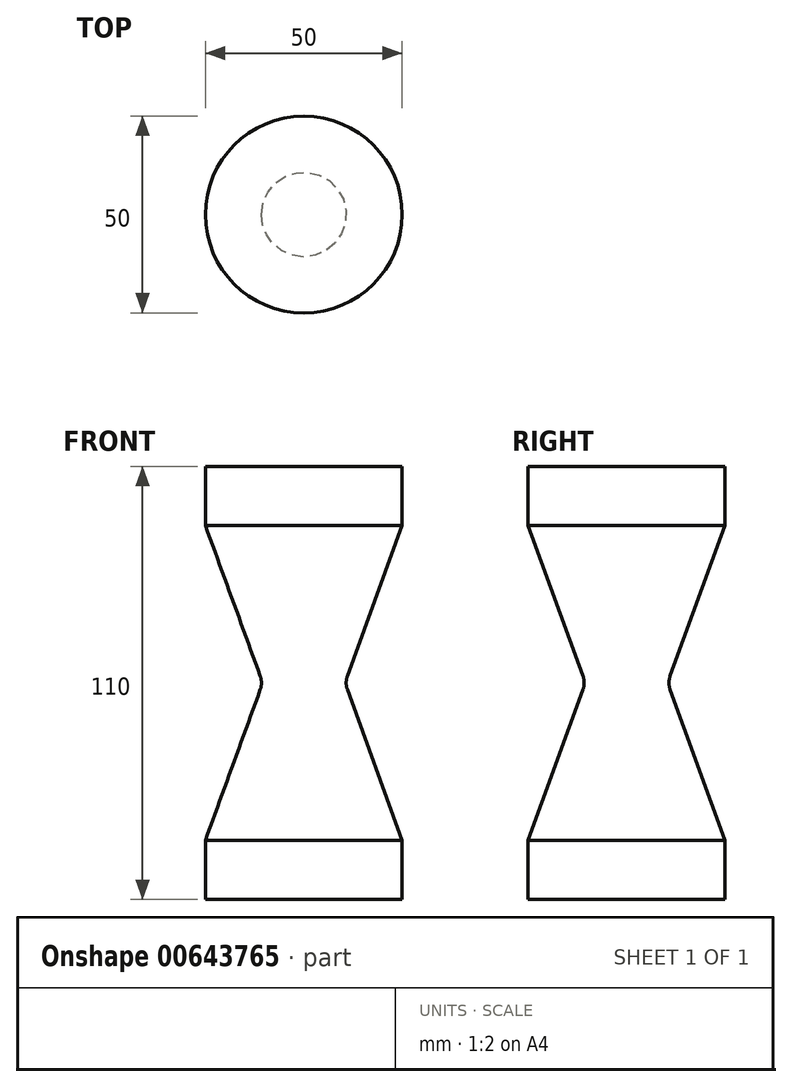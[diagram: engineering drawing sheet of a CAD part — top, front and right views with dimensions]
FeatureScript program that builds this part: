
annotation { "Feature Type Name" : "Feature", "Feature Type Description" : "" }
export const myFeature = defineFeature(function(context is Context, id is Id, definition is map)
    precondition{}
    {
        {
            var Q0;
            Q0=qCreatedBy(makeId("Front.planeOp"),FACE);
            var sketch = newSketch(context, id + "F0", { "sketchPlane" : qUnion([Q0])});
            skLineSegment(sketch, "E0", {"start": v(0, 0) * mm, "end": v(0, 110) * mm});
            skLineSegment(sketch, "E1", {"start": v(0, 0) * mm, "end": v(25, 0) * mm});
            skLineSegment(sketch, "E2", {"start": v(25, 0) * mm, "end": v(25, 15) * mm});
            skLineSegment(sketch, "E3", {"start": v(25, 15) * mm, "end": v(10.44, 55) * mm});
            skPoint(sketch, "E3.endSnap0", {"position": v(0, 55) * mm});
            skLineSegment(sketch, "E4", {"start": v(0, 55) * mm, "end": v(6.55, 55) * mm, "construction": true});
            skLineSegment(sketch, "E5.MirrorCS", {"start": v(25, 95) * mm, "end": v(10.44, 55) * mm});
            skLineSegment(sketch, "E6.MirrorCS", {"start": v(25, 110) * mm, "end": v(25, 95) * mm});
            skLineSegment(sketch, "E7.MirrorCS", {"start": v(0, 110) * mm, "end": v(25, 110) * mm});
            skSolve(sketch);
        }
        {
            var Q0;
            Q0 = qSketchRegion(id + "F0", true);
            var Q1;
            Q1=sQuery(id+"F0.wireOp",EDGE,"E0");
            revolve(context, id + "F1", {"entities" : qUnion([Q0]), "axis" : qUnion([Q1]), "revolveType" : RevolveType.FULL});
        }
        {
            var Q0;
            Q0=makeQuery(id+"F1.opRevolve","SWEPT_EDGE",EDGE,{"disambiguationData":[OSD([sQuery(id+"F0.wireOp",EDGE,"E3"),sQuery(id+"F0.wireOp",EDGE,"E5.MirrorCS")])]});
            fillet(context, id + "F2", {"entities" : qUnion([Q0]), "radius" : 5 * mm, "tangentPropagation" : true, "allowEdgeOverflow" : false});
        }
    });
